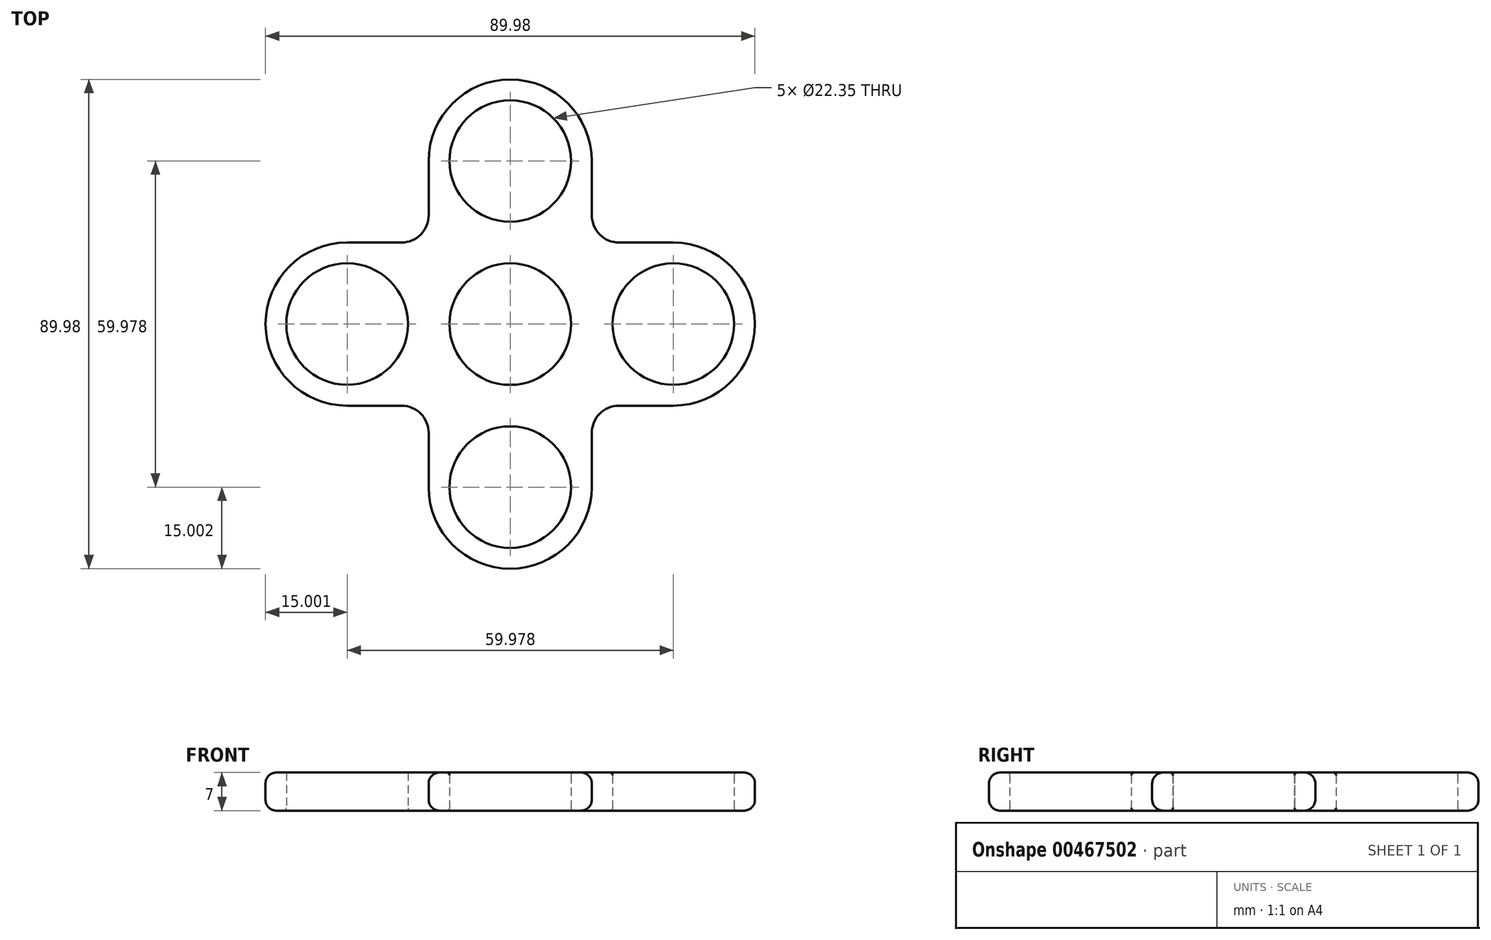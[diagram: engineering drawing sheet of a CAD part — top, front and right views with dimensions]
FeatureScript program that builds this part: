
annotation { "Feature Type Name" : "Feature", "Feature Type Description" : "" }
export const myFeature = defineFeature(function(context is Context, id is Id, definition is map)
    precondition{}
    {
        {
            var Q0;
            Q0=qCreatedBy(makeId("Top.planeOp"),FACE);
            var sketch = newSketch(context, id + "F0", { "sketchPlane" : qUnion([Q0])});
            skCircle(sketch, "E0", {"center": v(0, 30) * mm, "radius": 11.18 * mm});
            skLineSegment(sketch, "E1", {"start": v(0, 0) * mm, "end": v(0, 30) * mm, "construction": true});
            skCircle(sketch, "E2", {"center": v(0, 30) * mm, "radius": 15 * mm});
            skCircle(sketch, "E3", {"center": v(0, 0) * mm, "radius": 11.18 * mm});
            skLineSegment(sketch, "E4", {"start": v(-15, 30) * mm, "end": v(-15, 0) * mm});
            skLineSegment(sketch, "E5", {"start": v(15, 30) * mm, "end": v(15, 0) * mm});
            skLineSegment(sketch, "E6", {"start": v(-15, 0) * mm, "end": v(15, 0) * mm});
            skLineSegment(sketch, "E7.1.0", {"start": v(-29.99, -14.99) * mm, "end": v(0.01, -14.99) * mm});
            skCircle(sketch, "E7.1.1", {"center": v(-29.99, 0.01) * mm, "radius": 15 * mm});
            skCircle(sketch, "E7.1.2", {"center": v(-29.99, 0.01) * mm, "radius": 11.18 * mm});
            skLineSegment(sketch, "E7.1.3", {"start": v(-29.99, 15.01) * mm, "end": v(0.01, 15.01) * mm});
            skPoint(sketch, "E7.1.4", {"position": v(0.01, 0.01) * mm});
            skLineSegment(sketch, "E7.2.0", {"start": v(15, -29.98) * mm, "end": v(15, 0.02) * mm});
            skCircle(sketch, "E7.2.1", {"center": v(0, -29.98) * mm, "radius": 15 * mm});
            skCircle(sketch, "E7.2.2", {"center": v(0, -29.98) * mm, "radius": 11.18 * mm});
            skLineSegment(sketch, "E7.2.3", {"start": v(-15, -29.98) * mm, "end": v(-15, 0.02) * mm});
            skPoint(sketch, "E7.2.4", {"position": v(0, 0.02) * mm});
            skLineSegment(sketch, "E7.3.0", {"start": v(29.99, 15.01) * mm, "end": v(-0.01, 15.01) * mm});
            skCircle(sketch, "E7.3.1", {"center": v(29.99, 0.01) * mm, "radius": 15 * mm});
            skCircle(sketch, "E7.3.2", {"center": v(29.99, 0.01) * mm, "radius": 11.18 * mm});
            skLineSegment(sketch, "E7.3.3", {"start": v(29.99, -14.99) * mm, "end": v(-0.01, -14.99) * mm});
            skPoint(sketch, "E7.3.4", {"position": v(-0.01, 0.01) * mm});
            skPoint(sketch, "E7.center", {"position": v(0, 0.01) * mm});
            skSolve(sketch);
        }
        {
            var Q0;
            Q0=makeQuery(id+"F0.imprint","IMPRINT",FACE,{"disambiguationData":[TD([[makeQuery(id+"F0.imprint","IMPRINT",EDGE,{"derivedFrom":sQuery(id+"F0.wireOp",EDGE,"36e7d391-d642-43d3-ac27-a5ee1db5424b.1.0")}),-1.0]])]});
            var Q1;
            {var subQ0=sQuery(id+"F0.wireOp",EDGE,"E6");var subQ1=sQuery(id+"F0.wireOp",EDGE,"E3");var subQ2=makeQuery(id+"F0.imprint","INTERSECT",VERTEX,{"disambiguationData":[OD(0.0)],"derivedFrom":[subQ1,subQ0]});Q1=makeQuery(id+"F0.imprint","IMPRINT",FACE,{"disambiguationData":[TD([[makeQuery(id+"F0.imprint","IMPRINT",EDGE,{"disambiguationData":[TD([[subQ2,-1.0]])],"derivedFrom":subQ1}),-1.0]])]});}
            var Q2;
            Q2=makeQuery(id+"F0.imprint","IMPRINT",FACE,{"disambiguationData":[TD([[makeQuery(id+"F0.imprint","IMPRINT",EDGE,{"derivedFrom":sQuery(id+"F0.wireOp",EDGE,"36e7d391-d642-43d3-ac27-a5ee1db5424b.2.0")}),-1.0]])]});
            var Q3;
            {var subQ0=sQuery(id+"F0.wireOp",EDGE,"E4");var subQ1=sQuery(id+"F0.wireOp",EDGE,"E2");var subQ2=makeQuery(id+"F0.imprint","INTERSECT",VERTEX,{"derivedFrom":[subQ1,subQ0]});Q3=makeQuery(id+"F0.imprint","IMPRINT",FACE,{"disambiguationData":[TD([[makeQuery(id+"F0.imprint","IMPRINT",EDGE,{"disambiguationData":[TD([[subQ2,-1.0]])],"derivedFrom":subQ1}),-1.0]])]});}
            var Q4;
            Q4=makeQuery(id+"F0.imprint","IMPRINT",FACE,{"disambiguationData":[TD([[makeQuery(id+"F0.imprint","IMPRINT",EDGE,{"derivedFrom":sQuery(id+"F0.wireOp",EDGE,"E0")}),-1.0]])]});
            var Q5;
            Q5=makeQuery(id+"F0.imprint","IMPRINT",FACE,{"disambiguationData":[TD([[makeQuery(id+"F0.imprint","IMPRINT",EDGE,{"derivedFrom":sQuery(id+"F0.wireOp",EDGE,"E7.1.2")}),-1.0]])]});
            var Q6;
            {var subQ10=sQuery(id+"F0.wireOp",EDGE,"E7.1.3");var subQ15=sQuery(id+"F0.wireOp",EDGE,"E2");var subQ16=makeQuery(id+"F0.imprint","INTERSECT",VERTEX,{"derivedFrom":[subQ15,subQ10]});Q6=makeQuery(id+"F0.imprint","IMPRINT",FACE,{"disambiguationData":[TD([[makeQuery(id+"F0.imprint","IMPRINT",EDGE,{"disambiguationData":[TD([[subQ16,-1.0]])],"derivedFrom":subQ15}),-1.0]])]});}
            var Q7;
            {var subQ0=sQuery(id+"F0.wireOp",EDGE,"E7.1.3");var subQ6=makeQuery(id+"F0.imprint","IMPRINT",VERTEX,{"derivedFrom":subQ0});Q7=makeQuery(id+"F0.imprint","IMPRINT",FACE,{"disambiguationData":[TD([[makeQuery(id+"F0.imprint","IMPRINT",EDGE,{"disambiguationData":[TD([[subQ6,1.0]])],"derivedFrom":subQ0}),-1.0]])]});}
            var Q8;
            {var subQ0=sQuery(id+"F0.wireOp",EDGE,"E4");var subQ1=makeQuery(id+"F0.imprint","IMPRINT",VERTEX,{"derivedFrom":subQ0});Q8=makeQuery(id+"F0.imprint","IMPRINT",FACE,{"disambiguationData":[TD([[makeQuery(id+"F0.imprint","IMPRINT",EDGE,{"disambiguationData":[TD([[subQ1,1.0]])],"derivedFrom":subQ0}),1.0]])]});}
            var Q9;
            {var subQ1=sQuery(id+"F0.wireOp",EDGE,"E6");var subQ3=sQuery(id+"F0.wireOp",EDGE,"E7.1.1");var subQ4=makeQuery(id+"F0.imprint","INTERSECT",VERTEX,{"derivedFrom":[subQ1,subQ3]});Q9=makeQuery(id+"F0.imprint","IMPRINT",FACE,{"disambiguationData":[TD([[makeQuery(id+"F0.imprint","IMPRINT",EDGE,{"disambiguationData":[TD([[subQ4,1.0]])],"derivedFrom":subQ3}),1.0]])]});}
            var Q10;
            Q10=makeQuery(id+"F0.imprint","IMPRINT",FACE,{"disambiguationData":[TD([[makeQuery(id+"F0.imprint","IMPRINT",EDGE,{"derivedFrom":sQuery(id+"F0.wireOp",EDGE,"E7.3.2")}),-1.0]])]});
            var Q11;
            {var subQ0=sQuery(id+"F0.wireOp",EDGE,"E7.3.3");var subQ1=sQuery(id+"F0.wireOp",EDGE,"E7.2.0");var subQ2=makeQuery(id+"F0.imprint","INTERSECT",VERTEX,{"derivedFrom":[subQ1,subQ0]});Q11=makeQuery(id+"F0.imprint","IMPRINT",FACE,{"disambiguationData":[TD([[makeQuery(id+"F0.imprint","IMPRINT",EDGE,{"disambiguationData":[TD([[subQ2,-1.0]])],"derivedFrom":subQ1}),-1.0]])]});}
            var Q12;
            {var subQ1=sQuery(id+"F0.wireOp",EDGE,"E6");var subQ3=sQuery(id+"F0.wireOp",EDGE,"E7.3.1");var subQ4=makeQuery(id+"F0.imprint","INTERSECT",VERTEX,{"derivedFrom":[subQ1,subQ3]});Q12=makeQuery(id+"F0.imprint","IMPRINT",FACE,{"disambiguationData":[TD([[makeQuery(id+"F0.imprint","IMPRINT",EDGE,{"disambiguationData":[TD([[subQ4,-1.0]])],"derivedFrom":subQ3}),1.0]])]});}
            var Q13;
            {var subQ0=sQuery(id+"F0.wireOp",EDGE,"E5");var subQ1=makeQuery(id+"F0.imprint","IMPRINT",VERTEX,{"derivedFrom":subQ0});Q13=makeQuery(id+"F0.imprint","IMPRINT",FACE,{"disambiguationData":[TD([[makeQuery(id+"F0.imprint","IMPRINT",EDGE,{"disambiguationData":[TD([[subQ1,1.0]])],"derivedFrom":subQ0}),-1.0]])]});}
            var Q14;
            {var subQ0=sQuery(id+"F0.wireOp",EDGE,"E7.3.0");var subQ1=sQuery(id+"F0.wireOp",EDGE,"E5");var subQ2=makeQuery(id+"F0.imprint","INTERSECT",VERTEX,{"derivedFrom":[subQ1,subQ0]});Q14=makeQuery(id+"F0.imprint","IMPRINT",FACE,{"disambiguationData":[TD([[makeQuery(id+"F0.imprint","IMPRINT",EDGE,{"disambiguationData":[TD([[subQ2,-1.0]])],"derivedFrom":subQ1}),1.0]])]});}
            var Q15;
            {var subQ0=sQuery(id+"F0.wireOp",EDGE,"E5");var subQ1=sQuery(id+"F0.wireOp",EDGE,"E2");var subQ2=makeQuery(id+"F0.imprint","INTERSECT",VERTEX,{"derivedFrom":[subQ1,subQ0]});Q15=makeQuery(id+"F0.imprint","IMPRINT",FACE,{"disambiguationData":[TD([[makeQuery(id+"F0.imprint","IMPRINT",EDGE,{"disambiguationData":[TD([[subQ2,1.0]])],"derivedFrom":subQ1}),-1.0]])]});}
            var Q16;
            Q16=makeQuery(id+"F0.imprint","IMPRINT",FACE,{"disambiguationData":[TD([[makeQuery(id+"F0.imprint","IMPRINT",EDGE,{"derivedFrom":sQuery(id+"F0.wireOp",EDGE,"E7.2.2")}),-1.0]])]});
            var Q17;
            {var subQ0=sQuery(id+"F0.wireOp",EDGE,"E7.2.1");var subQ1=sQuery(id+"F0.wireOp",EDGE,"E7.2.0");var subQ2=makeQuery(id+"F0.imprint","INTERSECT",VERTEX,{"derivedFrom":[subQ1,subQ0]});Q17=makeQuery(id+"F0.imprint","IMPRINT",FACE,{"disambiguationData":[TD([[makeQuery(id+"F0.imprint","IMPRINT",EDGE,{"disambiguationData":[TD([[subQ2,-1.0]])],"derivedFrom":subQ1}),1.0]])]});}
            var Q18;
            {var subQ0=sQuery(id+"F0.wireOp",EDGE,"E7.1.0");var subQ1=makeQuery(id+"F0.imprint","IMPRINT",VERTEX,{"derivedFrom":subQ0});Q18=makeQuery(id+"F0.imprint","IMPRINT",FACE,{"disambiguationData":[TD([[makeQuery(id+"F0.imprint","IMPRINT",EDGE,{"disambiguationData":[TD([[subQ1,1.0]])],"derivedFrom":subQ0}),1.0]])]});}
            var Q19;
            {var subQ0=sQuery(id+"F0.wireOp",EDGE,"E7.2.3");var subQ1=sQuery(id+"F0.wireOp",EDGE,"E7.1.0");var subQ2=makeQuery(id+"F0.imprint","INTERSECT",VERTEX,{"derivedFrom":[subQ1,subQ0]});Q19=makeQuery(id+"F0.imprint","IMPRINT",FACE,{"disambiguationData":[TD([[makeQuery(id+"F0.imprint","IMPRINT",EDGE,{"disambiguationData":[TD([[subQ2,-1.0]])],"derivedFrom":subQ1}),-1.0]])]});}
            var Q20;
            {var subQ0=sQuery(id+"F0.wireOp",EDGE,"E7.1.1");var subQ1=sQuery(id+"F0.wireOp",EDGE,"E7.1.0");var subQ2=makeQuery(id+"F0.imprint","INTERSECT",VERTEX,{"derivedFrom":[subQ1,subQ0]});Q20=makeQuery(id+"F0.imprint","IMPRINT",FACE,{"disambiguationData":[TD([[makeQuery(id+"F0.imprint","IMPRINT",EDGE,{"disambiguationData":[TD([[subQ2,-1.0]])],"derivedFrom":subQ1}),1.0]])]});}
            var Q21;
            {var subQ0=sQuery(id+"F0.wireOp",EDGE,"E7.1.3");var subQ1=sQuery(id+"F0.wireOp",EDGE,"E4");var subQ2=makeQuery(id+"F0.imprint","INTERSECT",VERTEX,{"derivedFrom":[subQ1,subQ0]});Q21=makeQuery(id+"F0.imprint","IMPRINT",FACE,{"disambiguationData":[TD([[makeQuery(id+"F0.imprint","IMPRINT",EDGE,{"disambiguationData":[TD([[subQ2,-1.0]])],"derivedFrom":subQ1}),-1.0]])]});}
            extrude(context, id + "F1", {"entities" : qUnion([Q0, Q1, Q2, Q3, Q4, Q5, Q6, Q7, Q8, Q9, Q10, Q11, Q12, Q13, Q14, Q15, Q16, Q17, Q18, Q19, Q20, Q21]), "depth" : 7 * mm});
        }
        {
            var Q0;
            {var subQ0=sQuery(id+"F0.wireOp",EDGE,"E4");Q0=qUnion([makeQuery(id+"F1.opExtrude","SWEPT_EDGE",EDGE,{"disambiguationData":[OSD([sQuery(id+"F0.wireOp",EDGE,"E2"),subQ0])]}),makeQuery(id+"F1.opExtrude","SWEPT_EDGE",EDGE,{"disambiguationData":[OSD([subQ0,sQuery(id+"F0.wireOp",EDGE,"E7.1.3")])]})]);}
            var Q1;
            {var subQ0=sQuery(id+"F0.wireOp",EDGE,"E5");Q1=qUnion([makeQuery(id+"F1.opExtrude","SWEPT_EDGE",EDGE,{"disambiguationData":[OSD([sQuery(id+"F0.wireOp",EDGE,"E2"),subQ0])]}),makeQuery(id+"F1.opExtrude","SWEPT_EDGE",EDGE,{"disambiguationData":[OSD([subQ0,sQuery(id+"F0.wireOp",EDGE,"E7.3.0")])]})]);}
            var Q2;
            Q2=makeQuery(id+"F1.opExtrude","SWEPT_EDGE",EDGE,{"disambiguationData":[OSD([sQuery(id+"F0.wireOp",EDGE,"36e7d391-d642-43d3-ac27-a5ee1db5424b.1.3"),sQuery(id+"F0.wireOp",EDGE,"36e7d391-d642-43d3-ac27-a5ee1db5424b.2.2")])]});
            var Q3;
            Q3=makeQuery(id+"F1.opExtrude","SWEPT_EDGE",EDGE,{"disambiguationData":[OSD([sQuery(id+"F0.wireOp",EDGE,"E7.2.0"),sQuery(id+"F0.wireOp",EDGE,"E7.3.3")])]});
            var Q4;
            Q4=makeQuery(id+"F1.opExtrude","SWEPT_EDGE",EDGE,{"disambiguationData":[OSD([sQuery(id+"F0.wireOp",EDGE,"E7.1.0"),sQuery(id+"F0.wireOp",EDGE,"E7.2.3")])]});
            fillet(context, id + "F2", {"entities" : qUnion([Q0, Q1, Q2, Q3, Q4]), "radius" : 5 * mm, "tangentPropagation" : true, "allowEdgeOverflow" : false});
        }
        {
            var Q0;
            Q0=makeQuery(id+"F1.opExtrude","CAP_EDGE",EDGE,{"disambiguationData":[OSD([sQuery(id+"F0.wireOp",EDGE,"E0")])],"isStart":false});
            var Q1;
            Q1=makeQuery(id+"F1.opExtrude","CAP_EDGE",EDGE,{"disambiguationData":[OSD([sQuery(id+"F0.wireOp",EDGE,"E3")])],"isStart":false});
            var Q2;
            Q2=makeQuery(id+"F1.opExtrude","CAP_EDGE",EDGE,{"disambiguationData":[OSD([sQuery(id+"F0.wireOp",EDGE,"36e7d391-d642-43d3-ac27-a5ee1db5424b.1.0")])],"isStart":false});
            var Q3;
            Q3=makeQuery(id+"F1.opExtrude","CAP_EDGE",EDGE,{"disambiguationData":[OSD([sQuery(id+"F0.wireOp",EDGE,"36e7d391-d642-43d3-ac27-a5ee1db5424b.2.0")])],"isStart":false});
            var Q4;
            Q4=makeQuery(id+"F1.opExtrude","CAP_EDGE",EDGE,{"disambiguationData":[OSD([sQuery(id+"F0.wireOp",EDGE,"36e7d391-d642-43d3-ac27-a5ee1db5424b.1.0")])],"isStart":true});
            var Q5;
            Q5=makeQuery(id+"F1.opExtrude","CAP_EDGE",EDGE,{"disambiguationData":[OSD([sQuery(id+"F0.wireOp",EDGE,"E0")])],"isStart":true});
            var Q6;
            Q6=makeQuery(id+"F1.opExtrude","CAP_EDGE",EDGE,{"disambiguationData":[OSD([sQuery(id+"F0.wireOp",EDGE,"36e7d391-d642-43d3-ac27-a5ee1db5424b.2.0")])],"isStart":true});
            var Q7;
            Q7=makeQuery(id+"F1.opExtrude","CAP_EDGE",EDGE,{"disambiguationData":[OSD([sQuery(id+"F0.wireOp",EDGE,"E3")])],"isStart":true});
            var Q8;
            Q8=makeQuery(id+"F1.opExtrude","CAP_EDGE",EDGE,{"disambiguationData":[OSD([sQuery(id+"F0.wireOp",EDGE,"E7.2.2")])],"isStart":false});
            var Q9;
            Q9=makeQuery(id+"F1.opExtrude","CAP_EDGE",EDGE,{"disambiguationData":[OSD([sQuery(id+"F0.wireOp",EDGE,"E7.1.2")])],"isStart":true});
            var Q10;
            Q10=makeQuery(id+"F1.opExtrude","CAP_EDGE",EDGE,{"disambiguationData":[OSD([sQuery(id+"F0.wireOp",EDGE,"E7.3.2")])],"isStart":true});
            var Q11;
            Q11=makeQuery(id+"F1.opExtrude","CAP_EDGE",EDGE,{"disambiguationData":[OSD([sQuery(id+"F0.wireOp",EDGE,"E7.2.2")])],"isStart":true});
            var Q12;
            Q12=makeQuery(id+"F1.opExtrude","CAP_EDGE",EDGE,{"disambiguationData":[OSD([sQuery(id+"F0.wireOp",EDGE,"E7.3.2")])],"isStart":false});
            fillet(context, id + "F3", {"entities" : qUnion([Q0, Q1, Q2, Q3, Q4, Q5, Q6, Q7, Q8, Q9, Q10, Q11, Q12]), "radius" : .5 * mm, "tangentPropagation" : true, "allowEdgeOverflow" : false});
        }
        {
            var Q0;
            Q0=makeQuery(id+"F1.opExtrude","SWEPT_FACE",FACE,{"disambiguationData":[OSD([sQuery(id+"F0.wireOp",EDGE,"36e7d391-d642-43d3-ac27-a5ee1db5424b.1.3")])]});
            var Q1;
            Q1=makeQuery(id+"F2.opFillet","BLEND_FACE",FACE,{"disambiguationData":[OSD([sQuery(id+"F0.wireOp",EDGE,"36e7d391-d642-43d3-ac27-a5ee1db5424b.1.3"),sQuery(id+"F0.wireOp",EDGE,"36e7d391-d642-43d3-ac27-a5ee1db5424b.2.2")])]});
            var Q2;
            Q2=makeQuery(id+"F1.opExtrude","SWEPT_FACE",FACE,{"disambiguationData":[OSD([sQuery(id+"F0.wireOp",EDGE,"36e7d391-d642-43d3-ac27-a5ee1db5424b.2.2")])]});
            var Q3;
            Q3=makeQuery(id+"F1.opExtrude","SWEPT_FACE",FACE,{"disambiguationData":[OSD([sQuery(id+"F0.wireOp",EDGE,"36e7d391-d642-43d3-ac27-a5ee1db5424b.2.1")])]});
            var Q4;
            Q4=makeQuery(id+"F1.opExtrude","SWEPT_FACE",FACE,{"disambiguationData":[OSD([sQuery(id+"F0.wireOp",EDGE,"36e7d391-d642-43d3-ac27-a5ee1db5424b.1.1")])]});
            var Q5;
            Q5=makeQuery(id+"F1.opExtrude","SWEPT_FACE",FACE,{"disambiguationData":[OSD([sQuery(id+"F0.wireOp",EDGE,"36e7d391-d642-43d3-ac27-a5ee1db5424b.1.2")])]});
            var Q6;
            Q6=makeQuery(id+"F2.opFillet","BLEND_FACE",FACE,{"disambiguationData":[OSD([sQuery(id+"F0.wireOp",EDGE,"E4"),sQuery(id+"F0.wireOp",EDGE,"E7.1.3")])]});
            var Q7;
            Q7=makeQuery(id+"F1.opExtrude","SWEPT_FACE",FACE,{"disambiguationData":[OSD([sQuery(id+"F0.wireOp",EDGE,"E4")])]});
            var Q8;
            Q8=makeQuery(id+"F1.opExtrude","SWEPT_FACE",FACE,{"disambiguationData":[OSD([sQuery(id+"F0.wireOp",EDGE,"E2")])]});
            var Q9;
            Q9=makeQuery(id+"F1.opExtrude","SWEPT_FACE",FACE,{"disambiguationData":[OSD([sQuery(id+"F0.wireOp",EDGE,"E5")])]});
            var Q10;
            Q10=makeQuery(id+"F2.opFillet","BLEND_FACE",FACE,{"disambiguationData":[OSD([sQuery(id+"F0.wireOp",EDGE,"E5"),sQuery(id+"F0.wireOp",EDGE,"E7.3.0")])]});
            var Q11;
            Q11=makeQuery(id+"F1.opExtrude","SWEPT_FACE",FACE,{"disambiguationData":[OSD([sQuery(id+"F0.wireOp",EDGE,"36e7d391-d642-43d3-ac27-a5ee1db5424b.2.3")])]});
            var Q12;
            Q12=makeQuery(id+"F1.opExtrude","CAP_EDGE",EDGE,{"disambiguationData":[OSD([sQuery(id+"F0.wireOp",EDGE,"E7.2.1")])],"isStart":false});
            var Q13;
            Q13=makeQuery(id+"F1.opExtrude","CAP_EDGE",EDGE,{"disambiguationData":[OSD([sQuery(id+"F0.wireOp",EDGE,"E7.2.1")])],"isStart":true});
            fillet(context, id + "F4", {"entities" : qUnion([Q0, Q1, Q2, Q3, Q4, Q5, Q6, Q7, Q8, Q9, Q10, Q11, Q12, Q13]), "radius" : 2 * mm, "tangentPropagation" : true, "allowEdgeOverflow" : false});
        }
    });
